# Revit family: 005.1_Шкаф Altis моноблочный металлический - IP 55 - IK 10 - RAL 7035
name_source: partatom
category: Электрооборудование
revit_build: Autodesk Revit 2016 (Build: 20150506_1715(x64)
units: mm (PartAtom-declared; Revit-internal decimal feet)

## family parameters
Всегда вертикально = Да
Конфигурация панели = Два столбца, слева направо
На основе рабочей плоскости = Нет
Общий = Да
При загрузке вырезать с полостями = Нет
Размер круглого соединителя = Использовать диаметр
Тип детали = Щит
Точка расчета площади = Нет

## types (29) — shared parameters
URL = http://www.e-catalogue.legrand.ru
URL Бренд = http://www.e-catalogue.legrand.ru
URL Каталог = http://www.e-catalogue.legrand.ru
URL Монтажная инструкция = http://www.e-catalogue.legrand.ru
URL Сертификат = http://www.e-catalogue.legrand.ru
Бренд = Altis
Единица измерения = шт.
Класс защиты, IP = 55
Номер OmniClass = 21.04.50.20.30
Номер UniFormat = D5020.30.26.24.13
Номинальный ток А = 0 А
Производитель = Legrand
Размер короба = 0 мм
Самозатухание = 0 °C
Цвет основного материала = RAL 7035
zero-valued in all types: Количество модулей (max)

## per-type parameters (varying)
| type | Артикул | Высота | Глубина | Коэффициент мощности | Наименование в спецификации | Номинальная мощность | Номинальное напряжение | Полная мощность | Ширина |
| 2000x1200x600 мм - 2 двери | 47172 | 2000 мм | 600 мм | 0 | Шкаф Altis моноблочный металлический - IP 55 - IK 10 - RAL 7035 - 2000x1200x600 мм - 2 двери | 0 Вт | 0 В | 0 В·А | 1200 мм |
| 2000x800x600 мм - 1 дверь | 47171 | 2000 мм | 600 мм | 0 | Шкаф Altis моноблочный металлический - IP 55 - IK 10 - RAL 7035 - 2000x800x600 мм - 1 дверь | 0 Вт | 0 В | 0 В·А | 800 мм |
| 1800x800x600 мм - 1 дверь | 47170 | 1800 мм | 600 мм | 0 | Шкаф Altis моноблочный металлический - IP 55 - IK 10 - RAL 7035 - 1800x800x600 мм - 1 дверь | 0 Вт | 0 В | 0 В·А | 800 мм |
| 2000x1600x500 мм - 2 двери | 47148 | 2000 мм | 500 мм | 0 | Шкаф Altis моноблочный металлический - IP 55 - IK 10 - RAL 7035 - 2000x1600x500 мм - 2 двери | 0 Вт | 0 В | 0 В·А | 1600 мм |
| 2000x1200x500 мм - 2 двери | 47147 | 2000 мм | 500 мм | 0 | Шкаф Altis моноблочный металлический - IP 55 - IK 10 - RAL 7035 - 2000x1200x500 мм - 2 двери | 0 Вт | 0 В | 0 В·А | 1200 мм |
| 2000x1000x500 мм - 2 двери | 47146 | 2000 мм | 500 мм | 0 | Шкаф Altis моноблочный металлический - IP 55 - IK 10 - RAL 7035 - 2000x1000x500 мм - 2 двери | 0 Вт | 0 В | 0 В·А | 1000 мм |
| 2000x800x500 мм - 1 дверь | 47145 | 2000 мм | 500 мм | 0 | Шкаф Altis моноблочный металлический - IP 55 - IK 10 - RAL 7035 - 2000x800x500 мм - 1 дверь | 0 Вт | 0 В | 0 В·А | 800 мм |
| 1800x1600x500 мм - 2 двери | 47142 | 1800 мм | 500 мм | 0 | Шкаф Altis моноблочный металлический - IP 55 - IK 10 - RAL 7035 - 1800x1000x500 мм - 2 двери | 0 Вт | 0 В | 0 В·А | 1600 мм |
| 1800x1200x500 мм - 2 двери | 47143 | 1800 мм | 500 мм | 0 | Шкаф Altis моноблочный металлический - IP 55 - IK 10 - RAL 7035 - 1800x1200x500 мм - 2 двери | 0 Вт | 0 В | 0 В·А | 1200 мм |
| 1800x1000x500 мм - 2 двери | 47142 | 1800 мм | 500 мм | 0 | Шкаф Altis моноблочный металлический - IP 55 - IK 10 - RAL 7035 - 1800x1000x500 мм - 2 двери | 0 Вт | 0 В | 0 В·А | 1000 мм |
| 1800x800x500 мм - 1 дверь | 47141 | 1800 мм | 500 мм | 0 | Шкаф Altis моноблочный металлический - IP 55 - IK 10 - RAL 7035 - 1800x800x500 мм - 1 дверь | 0 Вт | 0 В | 0 В·А | 800 мм |
| 1800x600x500 мм - 1 дверь | 47140 | 1800 мм | 500 мм | 0 | Шкаф Altis моноблочный металлический - IP 55 - IK 10 - RAL 7035 - 1800x600x500 мм - 1 дверь | 0 Вт | 0 В | 0 В·А | 600 мм |
| 2000x1600x400 мм - 2 двери | 47136 | 2000 мм | 400 мм | 0 | Шкаф Altis моноблочный металлический - IP 55 - IK 10 - RAL 7035 - 2000x1600x400 мм - 2 двери | 0 Вт | 0 В | 0 В·А | 1600 мм |
| 2000x1200x400 мм - 2 двери | 47135 | 2000 мм | 400 мм | 0 | Шкаф Altis моноблочный металлический - IP 55 - IK 10 - RAL 7035 - 2000x1200x400 мм - 2 двери | 0 Вт | 0 В | 0 В·А | 1200 мм |
| 2000x1000x400 мм - 2 двери | 47134 | 2000 мм | 400 мм | 0 | Шкаф Altis моноблочный металлический - IP 55 - IK 10 - RAL 7035 - 2000x1000x400 мм - 2 двери | 0 Вт | 0 В | 0 В·А | 1000 мм |
| 2000x1000x400 мм - 1 дверь | 47133 | 2000 мм | 400 мм | 0 | Шкаф Altis моноблочный металлический - IP 55 - IK 10 - RAL 7035 - 2000x1000x400 мм - 1 дверь | 0 Вт | 0 В | 0 В·А | 1000 мм |
| 2000x800x400 мм - 1 дверь | 47132 | 2000 мм | 400 мм | 0 | Шкаф Altis моноблочный металлический - IP 55 - IK 10 - RAL 7035 - 2000x800x400 мм - 1 дверь | 0 Вт | 0 В | 0 В·А | 800 мм |
| 2000x600x400 мм - 1 дверь | 47131 | 2000 мм | 400 мм | 0 | Шкаф Altis моноблочный металлический - IP 55 - IK 10 - RAL 7035 - 2000x600x400 мм - 1 дверь | 0 Вт | 0 В | 0 В·А | 1600 мм |
| 1800x1600x400 мм - 2 двери | 47130 | 1800 мм | 400 мм | 0 | Шкаф Altis моноблочный металлический - IP 55 - IK 10 - RAL 7035 - 1800x1600x400 мм - 2 двери | 0 Вт | 0 В | 0 В·А | 1600 мм |
| 1800x1200x400 мм - 2 двери | 47129 | 1800 мм | 400 мм | 0 | Шкаф Altis моноблочный металлический - IP 55 - IK 10 - RAL 7035 - 1800x1200x400 мм - 2 двери | 0 Вт | 0 В | 0 В·А | 1200 мм |
| 1800x1000x400 мм - 2 двери | 47128 | 1800 мм | 400 мм | 0 | Шкаф Altis моноблочный металлический - IP 55 - IK 10 - RAL 7035 - 1800x1000x400 мм - 2 двери | 0 Вт | 0 В | 0 В·А | 1000 мм |
| 1800x1000x400 мм - 1 дверь | 47127 | 1800 мм | 400 мм | 0 | Шкаф Altis моноблочный металлический - IP 55 - IK 10 - RAL 7035 - 1800x1000x400 мм - 1 дверь | 0 Вт | 0 В | 0 В·А | 1000 мм |
| 1800x800x400 мм - 1 дверь | 47126 | 1800 мм | 400 мм | 0 | Шкаф Altis моноблочный металлический - IP 55 - IK 10 - RAL 7035 - 1800x800x400 мм - 1 дверь | 0 Вт | 0 В | 0 В·А | 800 мм |
| 1800x600x400 мм - 1 дверь | 47125 | 1800 мм | 400 мм | 0 | Шкаф Altis моноблочный металлический - IP 55 - IK 10 - RAL 7035 - 1800x600x400 мм - 1 дверь | 0 Вт | 0 В | 0 В·А | 600 мм |
| 1600x1200x400 мм - 2 двери | 47124 | 1600 мм | 400 мм | 1 | Шкаф Altis моноблочный металлический - IP 55 - IK 10 - RAL 7035 - 1600x1200x400 мм - 2 двери | 350 Вт | 400 В | 350 В·А | 1200 мм |
| 1600x1000x400 мм - 2 двери | 47123 | 1600 мм | 400 мм | 0 | Шкаф Altis моноблочный металлический - IP 55 - IK 10 - RAL 7035 - 1600x1000x400 мм - 2 двери | 0 Вт | 0 В | 0 В·А | 1000 мм |
| 1600x800x400 мм - 1 дверь | 47121 | 1600 мм | 400 мм | 0 | Шкаф Altis моноблочный металлический - IP 55 - IK 10 - RAL 7035 - 1600x800x400 мм - 1 дверь | 0 Вт | 0 В | 0 В·А | 800 мм |
| 1600x600x400 мм - 1 дверь | 47120 | 1600 мм | 400 мм | 0 | Шкаф Altis моноблочный металлический - IP 55 - IK 10 - RAL 7035 - 1600x600x400 мм - 1 дверь | 0 Вт | 0 В | 0 В·А | 600 мм |
| 1600x1000x400 мм - 1 дверь | 47122 | 1600 мм | 400 мм | 0 | Шкаф Altis моноблочный металлический - IP 55 - IK 10 - RAL 7035 - 1600x1000x400 мм - 1 дверь | 0 Вт | 0 В | 0 В·А | 1000 мм |
